# Revit family: PipeAccessories_ButterflyValve_CastIron_Watermark_Dura_Wafer_50-300mm
name_source: partatom
category: Pipe Accessories
units: mm (PartAtom-declared; Revit-internal decimal feet)

## family parameters
Always vertical = Yes
Cut with Voids When Loaded = No
OmniClass Number = 23.65.55.14.17
OmniClass Title = Adjusting/Controlling Valves for Liquid Services
Part Type = Valve - Breaks Into
Round Connector Dimension = Use Radius
Shared = No
Work Plane-Based = No

## types (9) — shared parameters
Assembly Code = D2090800
BodyMaterial = <By Category>
Hand Wheel Material = <By Category>
Manufacturer = Dura
Model Specification = BMA
Model Version = 2013-03
ModifiedIssue_ANZRS = 20130925.63 $
NATSPECWorkSection = TBC
OmniclassProducts = TBC
PneumaticMaterial = <By Category>
Square_H = 30 mm  [stored 0.0984252 ft]
URL = www.reece.com.au
Uniformat IIElements = TBC

## per-type parameters (varying)
| type | A | B | C | D | Description | DiscDiameter | E | K | Model | NominalRadius | NominalRadius2 | NominalRadius3 | NominalSize | ProductCode | SquareA | SquareK | Square_d | StemRodWidth | T | Type Comments | X | XX | Y |
| WaterM_Butterfly Valve1_50mm | 191 mm | 80 mm | 43 mm  [stored 0.141076 ft] | 263 mm | TBC | 57 mm | 134 mm | 150 mm | WaterM_Butterfly Valve_50mm | 25 mm  [stored 0.082021 ft] | 40 mm  [stored 0.131234 ft] | 55 mm  [stored 0.180446 ft] | 50 mm  [stored 0.164042 ft] | 1011510 | 11 mm  [stored 0.0360892 ft] | 28 mm | 7 mm  [stored 0.0229659 ft] | 17 mm | 12 mm  [stored 0.0393701 ft] | TBC | 70 mm  [stored 0.229659 ft] | 8 mm  [stored 0.0262467 ft] | 150 mm |
| WaterM_Butterfly Valve2_65mm | 205 mm | 91 mm | 45 mm  [stored 0.147638 ft] | 263 mm |  | 72 mm | 134 mm | 150 mm | WaterM_Butterfly Valve_65mm | 33 mm  [stored 0.108268 ft] | 48 mm | 63 mm | 65 mm  [stored 0.213255 ft] | 1011516 | 11 mm  [stored 0.0360892 ft] | 36 mm | 7 mm  [stored 0.0229659 ft] | 18 mm  [stored 0.0590551 ft] | 13 mm  [stored 0.0426509 ft] |  | 85 mm | 9 mm  [stored 0.0295276 ft] | 165 mm |
| WaterM_Butterfly Valve3_80mm | 211 mm | 95 mm | 46 mm  [stored 0.150919 ft] | 263 mm |  | 83 mm | 134 mm | 150 mm | WaterM_Butterfly Valve_80mm | 40 mm  [stored 0.131234 ft] | 55 mm  [stored 0.180446 ft] | 70 mm  [stored 0.229659 ft] | 80 mm | 1011522 | 11 mm  [stored 0.0360892 ft] | 42 mm  [stored 0.137795 ft] | 7 mm  [stored 0.0229659 ft] | 18 mm  [stored 0.0590551 ft] | 13 mm  [stored 0.0426509 ft] |  | 100 mm | 9 mm  [stored 0.0295276 ft] | 180 mm |
| WaterM_Butterfly Valve4_100mm | 230 mm | 115 mm | 52 mm | 263 mm |  | 102 mm | 134 mm | 150 mm | WaterM_Butterfly Valve_100mm | 50 mm  [stored 0.164042 ft] | 65 mm  [stored 0.213255 ft] | 80 mm | 100 mm | 1011528 | 14 mm  [stored 0.0459318 ft] | 51 mm | 9 mm  [stored 0.0295276 ft] | 21 mm  [stored 0.0688976 ft] | 14 mm  [stored 0.0459318 ft] |  | 120 mm | 10 mm  [stored 0.0328084 ft] | 200 mm |
| WaterM_Butterfly Valve5_125mm | 245 mm | 134 mm | 56 mm  [stored 0.183727 ft] | 263 mm |  | 128 mm | 134 mm | 150 mm | WaterM_Butterfly Valve_125mm | 63 mm | 78 mm | 93 mm | 125 mm | 1011534 | 14 mm  [stored 0.0459318 ft] | 64 mm | 9 mm  [stored 0.0295276 ft] | 23 mm  [stored 0.0754593 ft] | 14 mm  [stored 0.0459318 ft] |  | 145 mm | 12 mm  [stored 0.0393701 ft] | 225 mm |
| WaterM_Butterfly Valve6_150mm | 255 mm | 138 mm | 57 mm | 263 mm |  | 151 mm | 134 mm | 150 mm | WaterM_Butterfly Valve_150mm | 75 mm | 93 mm | 110 mm | 150 mm | 1011540 | 17 mm | 76 mm | 9 mm  [stored 0.0295276 ft] | 23 mm  [stored 0.0754593 ft] | 14 mm  [stored 0.0459318 ft] |  | 170 mm | 12 mm  [stored 0.0393701 ft] | 250 mm |
| WaterM_Butterfly Valve7_200mm | 271 mm | 174 mm | 60 mm  [stored 0.19685 ft] | 326 mm |  | 201 mm | 240 mm | 305 mm | WaterM_Butterfly Valve_200mm | 100 mm | 118 mm | 135 mm | 200 mm | 1011546 | 17 mm | 100 mm | 11 mm  [stored 0.0360892 ft] | 25 mm  [stored 0.082021 ft] | 14 mm  [stored 0.0459318 ft] |  | 220 mm | 13 mm  [stored 0.0426509 ft] | 300 mm |
| WaterM_Butterfly Valve8_250mm | 326 mm | 198 mm | 69 mm | 412 mm |  | 251 mm | 240 mm | 305 mm | WaterM_Butterfly Valve_250mm | 125 mm | 143 mm | 160 mm | 250 mm | 1011552 | 22 mm  [stored 0.0721785 ft] | 126 mm | 11 mm  [stored 0.0360892 ft] | 29 mm | 16 mm  [stored 0.0524934 ft] |  | 270 mm | 15 mm  [stored 0.0492126 ft] | 350 mm |
| WaterM_Butterfly Valve9_300mm | 366 mm | 234 mm | 80 mm | 412 mm |  | 301 mm | 257 mm | 305 mm | WaterM_Butterfly Valve_300mm | 150 mm | 170 mm | 190 mm | 300 mm | 1011558 | 22 mm  [stored 0.0721785 ft] | 150 mm | 11 mm  [stored 0.0360892 ft] | 35 mm  [stored 0.114829 ft] | 18 mm  [stored 0.0590551 ft] |  | 320 mm | 17 mm | 400 mm |

note: [stored X ft] marks values corroborated as IEEE doubles in the binary element streams (Revit-internal decimal feet)

## geometry (parser evidence)
native form markers: Sweep x21
no freeform markers — native parametric forms only
